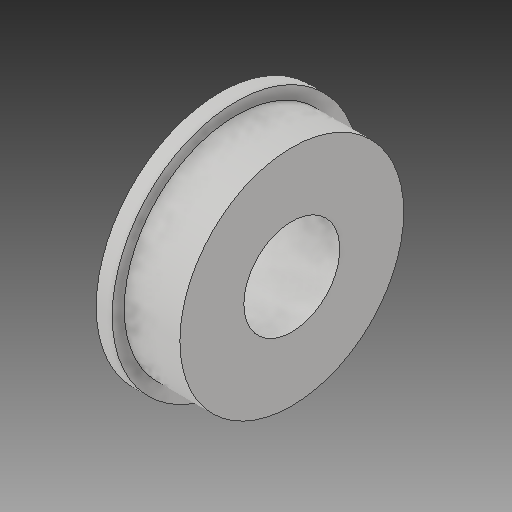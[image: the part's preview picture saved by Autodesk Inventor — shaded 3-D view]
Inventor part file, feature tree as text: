
AUTODESK INVENTOR PART (.ipt)
format: ipt  version: 2017 (Build 210142000, 142)  size: 122,880 bytes
history: native  units: in
note: dims shown in document units (in); Inventor stores cm internally (conversion verified against a paired STEP export)
features: revolve x1
ambient origin geometry x8: Origin, YZ Plane, XZ Plane, XY Plane, X Axis, Y Axis, Z Axis, Center Point
bodies: Solid1 (feature_tree)
feature tree (1):
  revolve  "Revolve1"  [1 undecoded]
note: 1 required parameter value undecoded (feature->parameter linkage not recoverable at this tier; creation-order binding heuristic only, values carry confidence <= 0.55)
